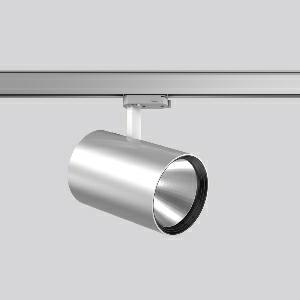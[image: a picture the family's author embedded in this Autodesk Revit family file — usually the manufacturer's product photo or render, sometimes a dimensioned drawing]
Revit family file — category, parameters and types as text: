
# Revit family: deecos_s_maxi_742242_004_2_d444
name_source: partatom
category: Lighting Fixtures
units: mm (PartAtom-declared; Revit-internal decimal feet)

## family parameters
Cut with Voids When Loaded = No
Host = Face
Light Source = No
Part Type = Normal
Room Calculation Point = No
Round Connector Dimension = Use Diameter
Shared = No

## types (1)
- DEECOS S maxi (1 x LED Modul 927 bakery, 3400 lm, 2700)
    Apparent Load = 33 VA
    Approval mark = CE
    CIE Flux Codes = 100 100 100 100 100
    Color Rendering = 90
    Color Temperature = 2700
    Default Elevation = 1800 mm
    Description = Series: DEECOS S maxi
LED surface-mounted projector in modern design with no visible cooling ribs. Housing: die-cast aluminium, powder-coated. Rotation range: 356°. Swivel range: 90°. Black plastic ring and recessed LED to prevent glare from the side. Optical assembly with reflector made of MIRO-Silver with 98% total light reflection for outstanding efficiency - can be changed without tools. Special LED for illumination of pastries included. With multi adaptor for 3-circuit tracks 230 V. Suitable for Track on ceiling, Wall track. High quality converter without flickering and stroboscopic effect. The following accessories can be mounted without use of tools: interchangeable lenses, decorative glasses, honeycomb louvre, clear and frosted diffusers, white interchangeable plastic ring. 
Colour: silver
Diameter: 123 mm
Height: 200 mm
Lamp: LED
Socket: without socket
Colour temperature: bakery
System power: 33 W
Rated luminous flux: 3400 lm
Luminous efficiency: 103 lm/W
Control gear: Regulated power supply
Protection class: I
Type of protection: IP 20
    Height = 200 mm  [stored 0.656168 ft]
    Lamp = 1 x LED Modul 927 bakery
    Lamp Light Flux = 3400 lm
    Lamp count = 1
    Length = 123 mm
    Lifetime = 50000 h
    Luminous efficacy = 103 lm/W
    Manufacturer = RZB
    ModVariant = No
    Model = 742242.004.2
    Mounting Place = Ceiling
    Mounting Type = Rail mounted
    Number of Poles = 1
    OnlyDefault = Yes
    Power Factor = 1
    Product Name = DEECOS S maxi
    Product group = Track mounted projectors
    ProductGroupID = 301
    Protection Class = Protection class I
    Protection Degree = IP 20
    RLX_Detail_Level = 1
    RLX_Emergency_Light_Flux = 0 lm
    RLX_Emergency_Type = 0
    RLX_Emergency_Type_DB = No
    RlxData = <blob elided: 40669 chars, md5=63bee05f>
    Socket = socket
    Standby Power = 0 W
    System Light Flux = 3400 lm
    System Power = 33 W
    Type Comments = Product without accessories
    Type Image = 741954.004.jpg
    URL = http://relux.com
    VarID = ---
    Voltage = 230 V
    Voltage Range = 220-240 V
    Weight = 0.00 kg
    Width = 0 mm  [stored 0 ft]

note: [stored X ft] marks values corroborated as IEEE doubles in the binary element streams (Revit-internal decimal feet)

## geometry (parser evidence)
native form markers: Blend x4, Sweep x13
no freeform markers — native parametric forms only
